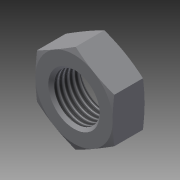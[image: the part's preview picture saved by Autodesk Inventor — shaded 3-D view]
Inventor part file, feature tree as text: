
AUTODESK INVENTOR PART (.ipt)
format: ipt  version: 2014 SP2 (Build 180246200, 246)  size: 157,184 bytes
history: native  units: in
note: dims shown in document units (in); Inventor stores cm internally (conversion verified against a paired STEP export)
features: other x70, sketch x3, revolve x2, extrude x1, thread x1
ambient origin geometry x8: Origin, YZ Plane, XZ Plane, XY Plane, X Axis, Y Axis, Z Axis, Center Point
bodies: Solid1 (feature_tree)
feature tree (77):
  sketch  "Sketch_8"  dims[d0=360.0deg d1=0.31in d2=0.0in]
  sketch  "Sketch_10"  dims[d3=360.0deg d4=0.2559in d5=0.0in]
  revolve  "Revolution1"  [1 undecoded]
  extrude  "Extrusion1"  Depth=0.2559in TaperAngle=0.0deg
  revolve  "Revolution2"  [1 undecoded]
  thread  "Thread1"  [1 undecoded]
  other  "NUT_XY"
  other  "NUT_YZ"
  other  "NUT_ZX"
  other  "NUT_X"
  other  "NUT_Y"
  other  "NUT_Z"
  other  "NUT_Center"
  other  "a1_XY"
  other  "a1_YZ"
  other  "a1_ZX"
  other  "a1_X"
  other  "a1_Y"
  other  "a1_Z"
  other  "a1_Center"
  other  "a2_XY"
  other  "a2_YZ"
  other  "a2_ZX"
  other  "a2_X"
  other  "a2_Y"
  other  "a2_Z"
  other  "a2_Center"
  other  "b1_XY"
  other  "b1_YZ"
  other  "b1_ZX"
  other  "b1_X"
  other  "b1_Y"
  other  "b1_Z"
  other  "b1_Center"
  other  "b2_XY"
  other  "b2_YZ"
  other  "b2_ZX"
  other  "b2_X"
  other  "b2_Y"
  other  "b2_Z"
  other  "b2_Center"
  other  "e_XY"
  other  "e_YZ"
  other  "e_ZX"
  other  "e_X"
  other  "e_Y"
  other  "e_Z"
  other  "e_Center"
  other  "ol1_XY"
  other  "ol1_YZ"
  other  "ol1_ZX"
  other  "ol1_X"
  other  "ol1_Y"
  other  "ol1_Z"
  other  "ol1_Center"
  other  "ol2_XY"
  other  "ol2_YZ"
  other  "ol2_ZX"
  other  "ol2_X"
  other  "ol2_Y"
  other  "ol2_Z"
  other  "ol2_Center"
  other  "th1_XY"
  other  "th1_YZ"
  other  "th1_ZX"
  other  "th1_X"
  other  "th1_Y"
  other  "th1_Z"
  other  "th1_Center"
  other  "th2_XY"
  other  "th2_YZ"
  other  "th2_ZX"
  other  "th2_X"
  other  "th2_Y"
  other  "th2_Z"
  other  "th2_Center"
  sketch  "Sketch_11"  dims[d6=0.0in d7=0.0in d8=0.0in]
note: 3 required parameter values undecoded (feature->parameter linkage not recoverable at this tier; creation-order binding heuristic only, values carry confidence <= 0.55)